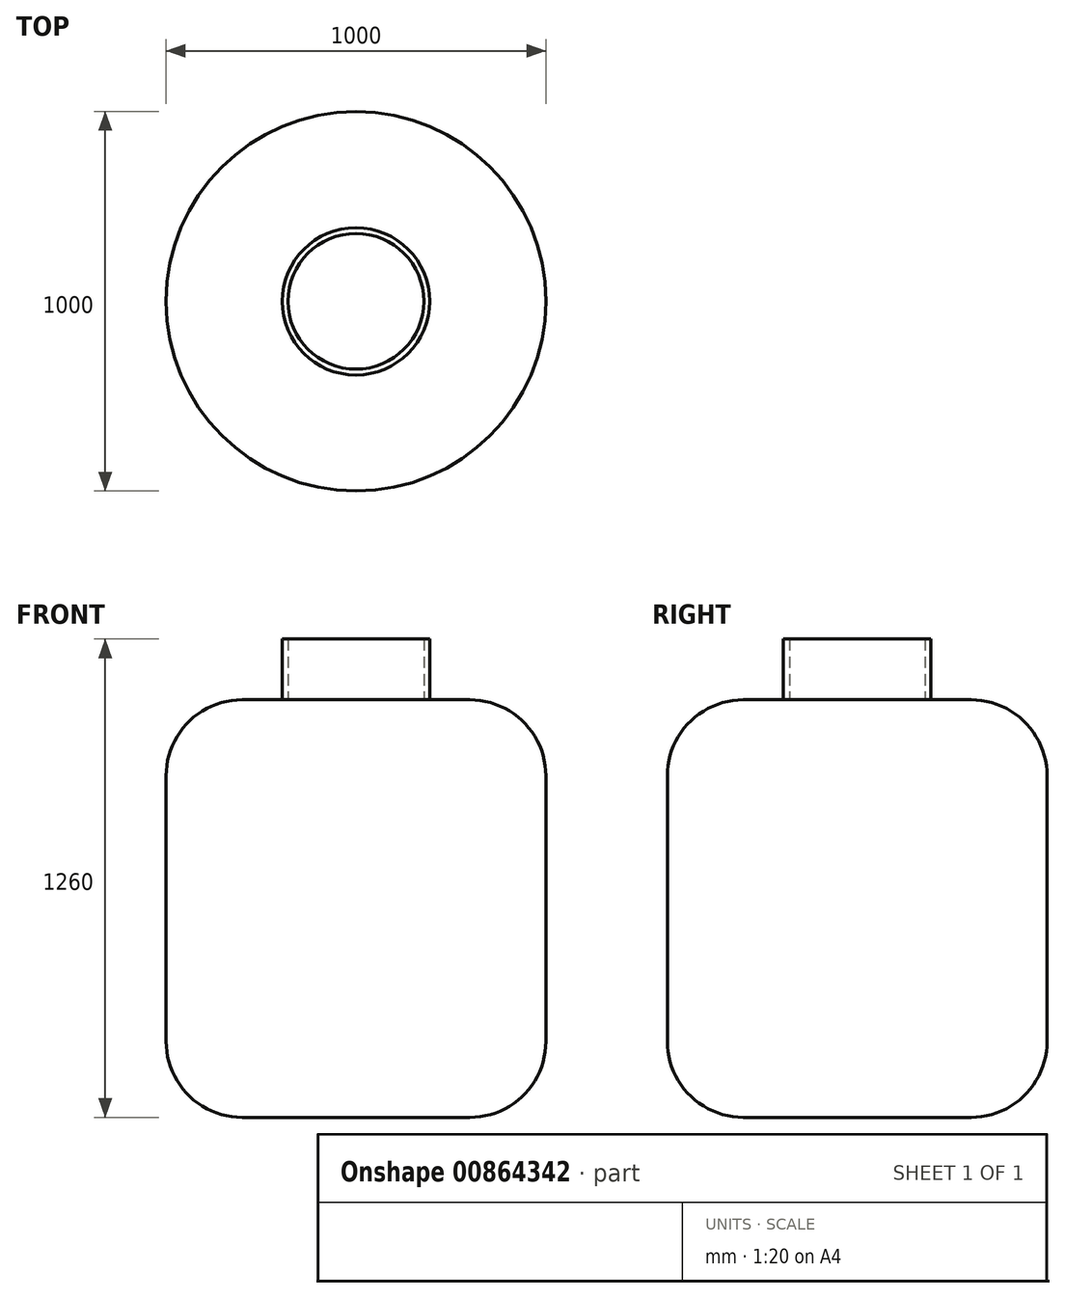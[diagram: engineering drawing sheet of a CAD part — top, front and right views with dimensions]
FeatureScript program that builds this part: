
annotation { "Feature Type Name" : "Feature", "Feature Type Description" : "" }
export const myFeature = defineFeature(function(context is Context, id is Id, definition is map)
    precondition{}
    {
        {
            var Q0;
            Q0=qCreatedBy(makeId("Top.planeOp"),FACE);
            var sketch = newSketch(context, id + "F0", { "sketchPlane" : qUnion([Q0])});
            skCircle(sketch, "E0", {"center": v(0, 0) * mm, "radius": 500 * mm});
            skSolve(sketch);
        }
        {
            var Q0;
            Q0=makeQuery(id+"F0.imprint","IMPRINT",FACE,{"disambiguationData":[TD([[makeQuery(id+"F0.imprint","IMPRINT",EDGE,{"derivedFrom":sQuery(id+"F0.wireOp",EDGE,"E0")}),1.0]])]});
            extrude(context, id + "F1", {"entities" : qUnion([Q0]), "depth" : 1100 * mm, "offsetDistance" : 25 * mm});
        }
        {
            var Q0;
            Q0=makeQuery(id+"F1.opExtrude","CAP_EDGE",EDGE,{"disambiguationData":[OSD([sQuery(id+"F0.wireOp",EDGE,"E0")])],"isStart":true});
            var Q1;
            Q1=makeQuery(id+"F1.opExtrude","CAP_EDGE",EDGE,{"disambiguationData":[OSD([sQuery(id+"F0.wireOp",EDGE,"E0")])],"isStart":false});
            fillet(context, id + "F2", {"entities" : qUnion([Q0, Q1]), "radius" : 200 * mm, "tangentPropagation" : true, "allowEdgeOverflow" : false});
        }
        {
            var Q0;
            Q0=makeQuery(id+"F1.opExtrude","CAP_FACE",FACE,{"disambiguationData":[OSD([sQuery(id+"F0.wireOp",EDGE,"E0")])],"isStart":false});
            var sketch = newSketch(context, id + "F3", { "sketchPlane" : qUnion([Q0])});
            skCircle(sketch, "E1", {"center": v(0, 0) * mm, "radius": 178.8 * mm});
            skCircle(sketch, "E2", {"center": v(0, 0) * mm, "radius": 194.13 * mm});
            skSolve(sketch);
        }
        {
            var Q0;
            Q0=makeQuery(id+"F3.imprint","IMPRINT",FACE,{"disambiguationData":[TD([[makeQuery(id+"F3.imprint","IMPRINT",EDGE,{"derivedFrom":sQuery(id+"F3.wireOp",EDGE,"E1")}),-1.0]])]});
            extrude(context, id + "F4", {"entities" : qUnion([Q0]), "operationType" : NewBodyOperationType.ADD, "depth" : 160 * mm, "offsetDistance" : 25 * mm});
        }
    });
